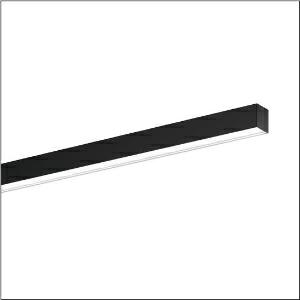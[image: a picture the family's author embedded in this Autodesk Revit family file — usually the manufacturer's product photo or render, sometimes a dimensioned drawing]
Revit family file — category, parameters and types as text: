
# Revit family: silica_21_51mx23tctab
name_source: partatom
category: Lighting Fixtures
units: mm (PartAtom-declared; Revit-internal decimal feet)

## family parameters
Cut with Voids When Loaded = No
Host = Face
Light Source = No
Part Type = Normal
Room Calculation Point = No
Round Connector Dimension = Use Diameter
Shared = No

## types (1)
- --- (1 x LED, 8070 lm, 81.1 W, 6500K)
    Apparent Load = 81 VA
    CIE Flux Codes = 78 96 99 100 100
    Color Rendering = 80
    Color Temperature = 6500K
    Default Elevation = 1800 mm
    Description = Silica 21, office luminaire, primary optical cover: prismatic diffuser, of PMMA, CAT 2 (L<= 3000cd/m²), light emission: direct distribution, primary light characteristic: symmetric, installation type: surface-mounted, LED, rated luminous flux: 8.070lm, luminous efficacy: 95lm/W, light colour: 8tw, colour temperature: 2700..6500K, control gear: DALI DT8, with terminal, 3+2-pole, max. 2.5mm², mains connection: 220..240V, AC, 50/60Hz, rated input power: 85.1W, luminaire housing, of aluminium, matt jet black (RAL 9005), length: 3.004mm, width: 53mm, height: 53mm, protection rating (complete): IP20, insulation class (complete): insulation class I (protective earthing), certification: CE, permissible operating ambient temperature: 0..+35°C, standard: EN 50419, packaging unit: 1 piece
    Height = 53 mm
    Lamp = 1 x LED
    Lamp Light Flux = 8070 lm
    Lamp Power = 81.1 W
    Lamp count = 1
    Length = 3004 mm
    Luminous efficacy = 100 lm/W
    Manufacturer = Siteco
    ModVariant = No
    Model = 51MX23TCTAB
    Mounting Place = Ceiling
    Mounting Type = Surface mounted
    Number of Poles = 1
    OnlyDefault = Yes
    Power Factor = 1
    Product Name = Silica 21
    Product group = office luminaire | ceiling mounted
    ProductGroupID = 301
    Protection Class = Protection class I
    Protection Degree = IP 20
    RLX_Detail_Level = 1
    RLX_Emergency_Light_Flux = 0 lm
    RLX_Emergency_Type = 0
    RLX_Emergency_Type_DB = No
    RlxData = <blob elided: 20341 chars, md5=3161a51d>
    Socket = socket
    Standby Power = 0 W
    System Light Flux = 8070 lm
    System Power = 81 W
    Type Comments = individual setting
    Type Image = l_1335925.jpg
    URL = http://relux.com
    VarID = @adj_140857
    Voltage = 0 V
    Weight = 0.00 kg
    Width = 53 mm

## geometry (parser evidence)
native form markers: Blend x4, Sweep x11
no freeform markers — native parametric forms only
